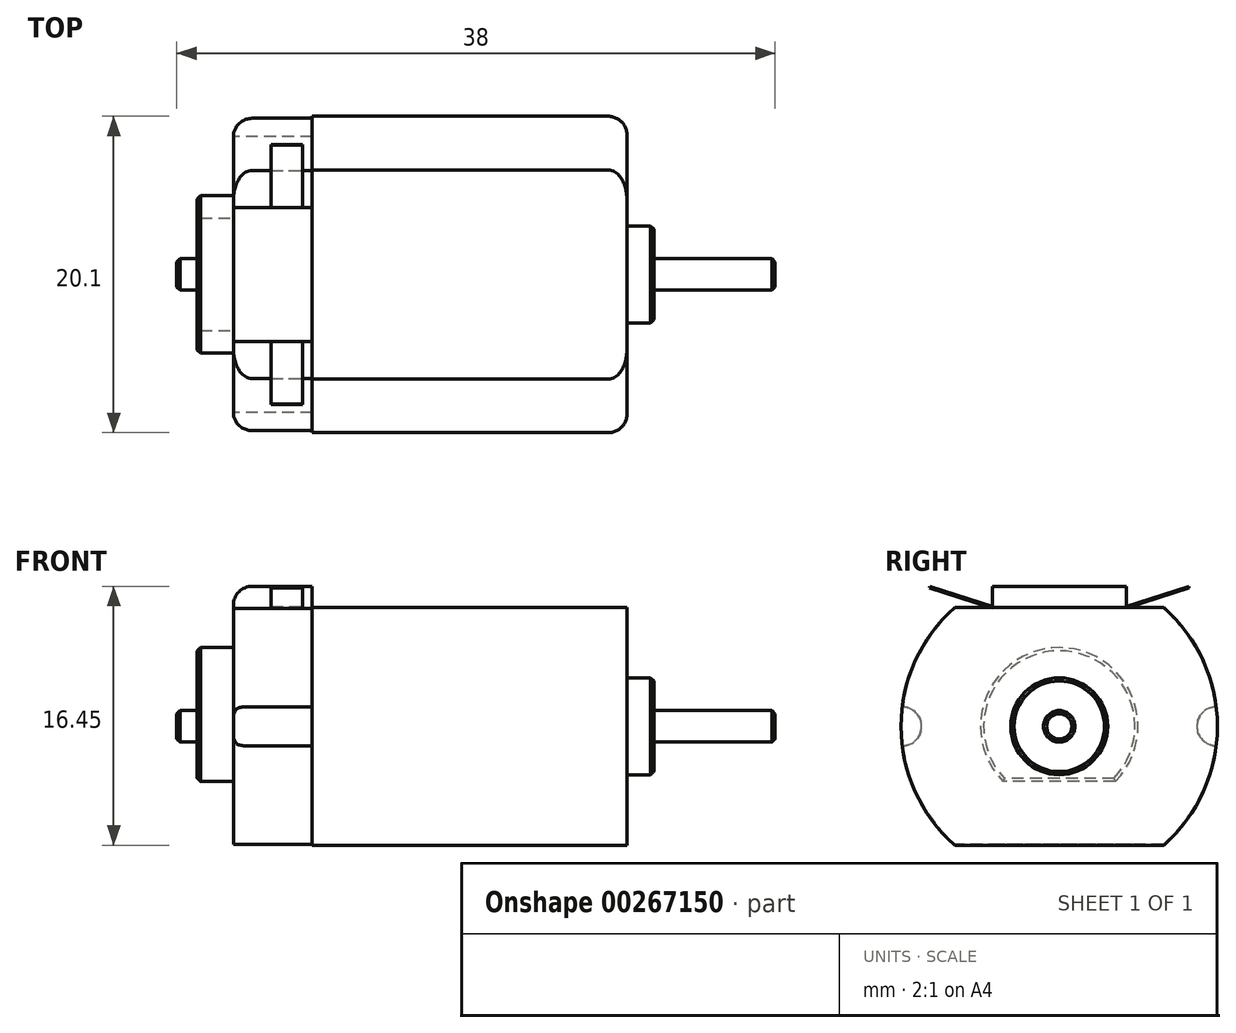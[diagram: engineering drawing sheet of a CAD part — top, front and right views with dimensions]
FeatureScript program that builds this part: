
annotation { "Feature Type Name" : "Feature", "Feature Type Description" : "" }
export const myFeature = defineFeature(function(context is Context, id is Id, definition is map)
    precondition{}
    {
        {
            var Q0;
            Q0=qCreatedBy(makeId("Right.planeOp"),FACE);
            var sketch = newSketch(context, id + "F0", { "sketchPlane" : qUnion([Q0])});
            skArc(sketch, "E0", {"start": v(-6.63, 7.55) * mm, "mid": v(-10.05, 0) * mm, "end": v(-6.63, -7.55) * mm});
            skLineSegment(sketch, "E1", {"start": v(-6.63, 7.55) * mm, "end": v(6.63, 7.55) * mm});
            skLineSegment(sketch, "E2", {"start": v(-6.63, -7.55) * mm, "end": v(6.63, -7.55) * mm});
            skArc(sketch, "E3.trimOffspring", {"start": v(6.63, -7.55) * mm, "mid": v(10.05, 0) * mm, "end": v(6.63, 7.55) * mm});
            skSolve(sketch);
        }
        {
            var Q0;
            Q0 = qSketchRegion(id + "F0", true);
            extrude(context, id + "F1", {"entities" : qUnion([Q0]), "depth" : 20 * mm});
        }
        {
            var Q0;
            Q0=makeQuery(id+"F1.opExtrude","CAP_FACE",FACE,{"disambiguationData":[OSD([sQuery(id+"F0.wireOp",EDGE,"E0"),sQuery(id+"F0.wireOp",EDGE,"E1"),sQuery(id+"F0.wireOp",EDGE,"E2"),sQuery(id+"F0.wireOp",EDGE,"E3.trimOffspring")])],"isStart":false});
            var sketch = newSketch(context, id + "F2", { "sketchPlane" : qUnion([Q0])});
            skCircle(sketch, "E4", {"center": v(0, 0) * mm, "radius": 3.08 * mm});
            skSolve(sketch);
        }
        {
            var Q0;
            Q0=makeQuery(id+"F2.imprint","IMPRINT",FACE,{"disambiguationData":[TD([[makeQuery(id+"F2.imprint","IMPRINT",EDGE,{"derivedFrom":sQuery(id+"F2.wireOp",EDGE,"E4")}),1.0]])]});
            extrude(context, id + "F3", {"entities" : qUnion([Q0]), "operationType" : NewBodyOperationType.ADD, "depth" : 1.7 * mm});
        }
        {
            var Q0;
            Q0=makeQuery(id+"F1.opExtrude","CAP_FACE",FACE,{"disambiguationData":[OSD([sQuery(id+"F0.wireOp",EDGE,"E0"),sQuery(id+"F0.wireOp",EDGE,"E1"),sQuery(id+"F0.wireOp",EDGE,"E2"),sQuery(id+"F0.wireOp",EDGE,"E3.trimOffspring")])],"isStart":true});
            var sketch = newSketch(context, id + "F4", { "sketchPlane" : qUnion([Q0])});
            skArc(sketch, "E5", {"start": v(-6.61, 7.5) * mm, "mid": v(-10, 0) * mm, "end": v(-6.61, -7.5) * mm});
            skLineSegment(sketch, "E6", {"start": v(-6.61, 7.5) * mm, "end": v(6.61, 7.5) * mm});
            skLineSegment(sketch, "E7", {"start": v(-6.61, -7.5) * mm, "end": v(6.61, -7.5) * mm});
            skArc(sketch, "E8.trimOffspring", {"start": v(6.61, -7.5) * mm, "mid": v(10, 0) * mm, "end": v(6.61, 7.5) * mm});
            skSolve(sketch);
        }
        {
            var Q0;
            Q0=makeQuery(id+"F4.imprint","IMPRINT",FACE,{"disambiguationData":[TD([[makeQuery(id+"F4.imprint","IMPRINT",EDGE,{"derivedFrom":sQuery(id+"F4.wireOp",EDGE,"E5")}),1.0]])]});
            extrude(context, id + "F5", {"entities" : qUnion([Q0]), "operationType" : NewBodyOperationType.ADD, "depth" : 5 * mm});
        }
        {
            var Q0;
            Q0=makeQuery(id+"F5.opExtrude","SWEPT_FACE",FACE,{"disambiguationData":[OSD([sQuery(id+"F4.wireOp",EDGE,"E6")])]});
            var sketch = newSketch(context, id + "F6", { "sketchPlane" : qUnion([Q0])});
            skLineSegment(sketch, "E9.bottom", {"start": v(-5, -4.25) * mm, "end": v(0, -4.25) * mm});
            skLineSegment(sketch, "E9.top", {"start": v(-5, 4.25) * mm, "end": v(0, 4.25) * mm});
            skLineSegment(sketch, "E9.left", {"start": v(-5, -4.25) * mm, "end": v(-5, 4.25) * mm});
            skLineSegment(sketch, "E9.right", {"start": v(0, -4.25) * mm, "end": v(0, 4.25) * mm});
            skSolve(sketch);
        }
        {
            var Q0;
            Q0=makeQuery(id+"F6.imprint","IMPRINT",FACE,{"disambiguationData":[TD([[makeQuery(id+"F6.imprint","IMPRINT",EDGE,{"derivedFrom":sQuery(id+"F6.wireOp",EDGE,"E9.bottom")}),1.0]])]});
            extrude(context, id + "F7", {"entities" : qUnion([Q0]), "operationType" : NewBodyOperationType.ADD, "depth" : 1.4 * mm});
        }
        {
            var Q0;
            Q0=makeQuery(id+"F7.boolean.opBoolean","MERGE",FACE,{"derivedFrom":[makeQuery(id+"F5.opExtrude","CAP_FACE",FACE,{"disambiguationData":[OSD([sQuery(id+"F4.wireOp",EDGE,"E5"),sQuery(id+"F4.wireOp",EDGE,"E6"),sQuery(id+"F4.wireOp",EDGE,"E7"),sQuery(id+"F4.wireOp",EDGE,"E8.trimOffspring")])],"isStart":false}),makeQuery(id+"F7.opExtrude","SWEPT_FACE",FACE,{"disambiguationData":[OSD([sQuery(id+"F6.wireOp",EDGE,"E9.left")])]})]});
            cPlane(context, id + "F8", {"entities" : qUnion([Q0]), "cplaneType" : CPlaneType.OFFSET, "offset" : 3.4 * mm, "oppositeDirection" : true, "width" : 150 * mm, "height" : 150 * mm});
        }
        {
            var Q0;
            Q0=qCreatedBy(id+"F8.planeOp",FACE);
            var sketch = newSketch(context, id + "F9", { "sketchPlane" : qUnion([Q0])});
            skPoint(sketch, "E10.0", {"position": v(4.25, 7.5) * mm});
            skLineSegment(sketch, "E11", {"start": v(4.25, 7.5) * mm, "end": v(4.25, 7.6) * mm});
            skLineSegment(sketch, "E12", {"start": v(4.25, 7.6) * mm, "end": v(8.22, 8.9) * mm});
            skLineSegment(sketch, "E13", {"start": v(8.22, 8.9) * mm, "end": v(8.25, 8.8) * mm});
            skLineSegment(sketch, "E14", {"start": v(8.25, 8.8) * mm, "end": v(4.25, 7.5) * mm});
            skPoint(sketch, "E15.0", {"position": v(-4.25, 7.5) * mm});
            skLineSegment(sketch, "E16", {"start": v(-4.25, 7.5) * mm, "end": v(-4.25, 7.6) * mm});
            skLineSegment(sketch, "E17", {"start": v(-4.25, 7.6) * mm, "end": v(-8.22, 8.9) * mm});
            skLineSegment(sketch, "E18", {"start": v(-8.22, 8.9) * mm, "end": v(-8.25, 8.8) * mm});
            skLineSegment(sketch, "E19", {"start": v(-8.25, 8.8) * mm, "end": v(-4.25, 7.5) * mm});
            skSolve(sketch);
        }
        {
            var Q0;
            Q0 = qSketchRegion(id + "F9", true);
            extrude(context, id + "F10", {"entities" : qUnion([Q0]), "operationType" : NewBodyOperationType.ADD, "depth" : 2 * mm, "symmetric" : true});
        }
        {
            var Q0;
            Q0=makeQuery(id+"F7.boolean.opBoolean","MERGE",FACE,{"derivedFrom":[makeQuery(id+"F5.opExtrude","CAP_FACE",FACE,{"disambiguationData":[OSD([sQuery(id+"F4.wireOp",EDGE,"E5"),sQuery(id+"F4.wireOp",EDGE,"E6"),sQuery(id+"F4.wireOp",EDGE,"E7"),sQuery(id+"F4.wireOp",EDGE,"E8.trimOffspring")])],"isStart":false}),makeQuery(id+"F7.opExtrude","SWEPT_FACE",FACE,{"disambiguationData":[OSD([sQuery(id+"F6.wireOp",EDGE,"E9.left")])]})]});
            var sketch = newSketch(context, id + "F11", { "sketchPlane" : qUnion([Q0])});
            skArc(sketch, "E20", {"start": v(3.57, -3.5) * mm, "mid": v(0, 5) * mm, "end": v(-3.57, -3.5) * mm});
            skLineSegment(sketch, "E21", {"start": v(-3.57, -3.5) * mm, "end": v(3.57, -3.5) * mm});
            skSolve(sketch);
        }
        {
            var Q0;
            Q0=makeQuery(id+"F11.imprint","IMPRINT",FACE,{"disambiguationData":[TD([[makeQuery(id+"F11.imprint","IMPRINT",EDGE,{"derivedFrom":sQuery(id+"F11.wireOp",EDGE,"E20")}),1.0]])]});
            extrude(context, id + "F12", {"entities" : qUnion([Q0]), "operationType" : NewBodyOperationType.ADD, "depth" : 2.3 * mm});
        }
        {
            var Q0;
            Q0=makeQuery(id+"F1.opExtrude","CAP_FACE",FACE,{"disambiguationData":[OSD([sQuery(id+"F0.wireOp",EDGE,"E0"),sQuery(id+"F0.wireOp",EDGE,"E1"),sQuery(id+"F0.wireOp",EDGE,"E2"),sQuery(id+"F0.wireOp",EDGE,"E3.trimOffspring")])],"isStart":false});
            var sketch = newSketch(context, id + "F13", { "sketchPlane" : qUnion([Q0])});
            skCircle(sketch, "E22", {"center": v(0, 0) * mm, "radius": 1 * mm});
            skSolve(sketch);
        }
        {
            var Q0;
            Q0 = qSketchRegion(id + "F13", true);
            extrude(context, id + "F14", {"entities" : qUnion([Q0]), "operationType" : NewBodyOperationType.ADD, "depth" : 9.4 * mm, "hasSecondDirection" : true, "secondDirectionOppositeDirection" : true, "secondDirectionDepth" : 28.6 * mm});
        }
        {
            var Q0;
            Q0=makeQuery(id+"F5.opExtrude","CAP_EDGE",EDGE,{"disambiguationData":[OSD([sQuery(id+"F4.wireOp",EDGE,"E8.trimOffspring")])],"isStart":false});
            var Q1;
            Q1=makeQuery(id+"F5.opExtrude","CAP_EDGE",EDGE,{"disambiguationData":[OSD([sQuery(id+"F4.wireOp",EDGE,"E5")])],"isStart":false});
            var Q2;
            Q2=makeQuery(id+"F7.opExtrude","CAP_EDGE",EDGE,{"disambiguationData":[OSD([sQuery(id+"F6.wireOp",EDGE,"E9.left")])],"isStart":false});
            var Q3;
            Q3=makeQuery(id+"F1.opExtrude","CAP_EDGE",EDGE,{"disambiguationData":[OSD([sQuery(id+"F0.wireOp",EDGE,"E0")])],"isStart":false});
            var Q4;
            Q4=makeQuery(id+"F1.opExtrude","CAP_EDGE",EDGE,{"disambiguationData":[OSD([sQuery(id+"F0.wireOp",EDGE,"E3.trimOffspring")])],"isStart":false});
            fillet(context, id + "F15", {"entities" : qUnion([Q0, Q1, Q2, Q3, Q4]), "radius" : 1.2 * mm, "tangentPropagation" : true, "allowEdgeOverflow" : false});
        }
        {
            var Q0;
            Q0=makeQuery(id+"F14.opExtrude","CAP_EDGE",EDGE,{"disambiguationData":[OSD([sQuery(id+"F13.wireOp",EDGE,"E22")])],"isStart":true});
            var Q1;
            Q1=makeQuery(id+"F12.opExtrude","CAP_EDGE",EDGE,{"disambiguationData":[OSD([sQuery(id+"F11.wireOp",EDGE,"E20")])],"isStart":false});
            var Q2;
            Q2=makeQuery(id+"F3.opExtrude","CAP_EDGE",EDGE,{"disambiguationData":[OSD([sQuery(id+"F2.wireOp",EDGE,"E4")])],"isStart":false});
            var Q3;
            Q3=makeQuery(id+"F14.opExtrude","CAP_EDGE",EDGE,{"disambiguationData":[OSD([sQuery(id+"F13.wireOp",EDGE,"E22")])],"isStart":false});
            var Q4;
            Q4=makeQuery(id+"F12.opExtrude","CAP_EDGE",EDGE,{"disambiguationData":[OSD([sQuery(id+"F11.wireOp",EDGE,"E21")])],"isStart":false});
            chamfer(context, id + "F16", {"entities" : qUnion([Q0, Q1, Q2, Q3, Q4]), "width" : 0.2 * mm, "tangentPropagation" : true});
        }
        {
            var Q0;
            Q0=makeQuery(id+"F7.boolean.opBoolean","MERGE",FACE,{"derivedFrom":[makeQuery(id+"F5.opExtrude","CAP_FACE",FACE,{"disambiguationData":[OSD([sQuery(id+"F4.wireOp",EDGE,"E5"),sQuery(id+"F4.wireOp",EDGE,"E6"),sQuery(id+"F4.wireOp",EDGE,"E7"),sQuery(id+"F4.wireOp",EDGE,"E8.trimOffspring")])],"isStart":false}),makeQuery(id+"F7.opExtrude","SWEPT_FACE",FACE,{"disambiguationData":[OSD([sQuery(id+"F6.wireOp",EDGE,"E9.left")])]})]});
            var sketch = newSketch(context, id + "F17", { "sketchPlane" : qUnion([Q0])});
            skLineSegment(sketch, "E23", {"start": v(0, 0) * mm, "end": v(10, 0) * mm, "construction": true});
            skArc(sketch, "E24", {"start": v(10, 1.25) * mm, "mid": v(8.75, 0) * mm, "end": v(10, -1.25) * mm});
            skLineSegment(sketch, "E25", {"start": v(10, 1.25) * mm, "end": v(12, 1.25) * mm});
            skLineSegment(sketch, "E26", {"start": v(10, -1.25) * mm, "end": v(12, -1.25) * mm});
            skLineSegment(sketch, "E27", {"start": v(12, 1.25) * mm, "end": v(12, -1.25) * mm});
            skLineSegment(sketch, "E28", {"start": v(0, 0) * mm, "end": v(-10, 0) * mm, "construction": true});
            skArc(sketch, "E29", {"start": v(-10, -1.25) * mm, "mid": v(-8.75, 0) * mm, "end": v(-10, 1.25) * mm});
            skLineSegment(sketch, "E30", {"start": v(-10, 1.25) * mm, "end": v(-12, 1.25) * mm});
            skLineSegment(sketch, "E31", {"start": v(-12, 1.25) * mm, "end": v(-12, -1.25) * mm});
            skLineSegment(sketch, "E32", {"start": v(-10, -1.25) * mm, "end": v(-12, -1.25) * mm});
            skSolve(sketch);
        }
        {
            var Q0;
            Q0 = qSketchRegion(id + "F17", true);
            extrude(context, id + "F18", {"entities" : qUnion([Q0]), "operationType" : NewBodyOperationType.REMOVE, "oppositeDirection" : true, "depth" : 5 * mm});
        }
    });
